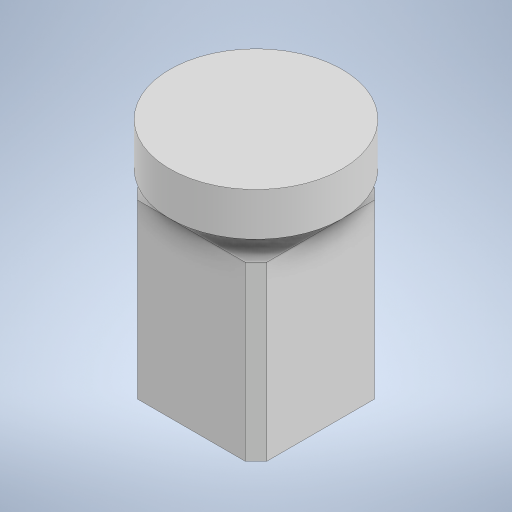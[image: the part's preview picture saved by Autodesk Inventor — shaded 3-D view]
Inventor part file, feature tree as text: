
AUTODESK INVENTOR PART (.ipt)
format: ipt  version: 2023 (Build 270158030, 158C)  size: 233,472 bytes
history: native  units: in
note: dims shown in document units (in); Inventor stores cm internally (conversion verified against a paired STEP export)
features: extrude x3, sketch x3
ambient origin geometry x8: Origin, YZ Plane, XZ Plane, XY Plane, X Axis, Y Axis, Z Axis, Center Point
bodies: Solid1 (feature_tree)
feature tree (6):
  extrude  "Extrusion1"  Depth=3.0in
  extrude  "Extrusion2"  Depth=0.25in
  extrude  "Extrusion3"  Depth=0.25in
  sketch  "Sketch1"  dims[d2=3.0in d3=3.0in]
  sketch  "Sketch2"  dims[d4=0.25in d5=0.25in]
  sketch  "Sketch3"  dims[d6=0.25in d7=0.25in d8=0.25in d9=0.25in d10=0.25in d11=0.25in d12=4.0in d13=0.0in d14=1.5in d15=1.5in d16=1.5in d17=0.5in d18=0.0in d19=4.0in d20=1.0in d21=0.0in]
